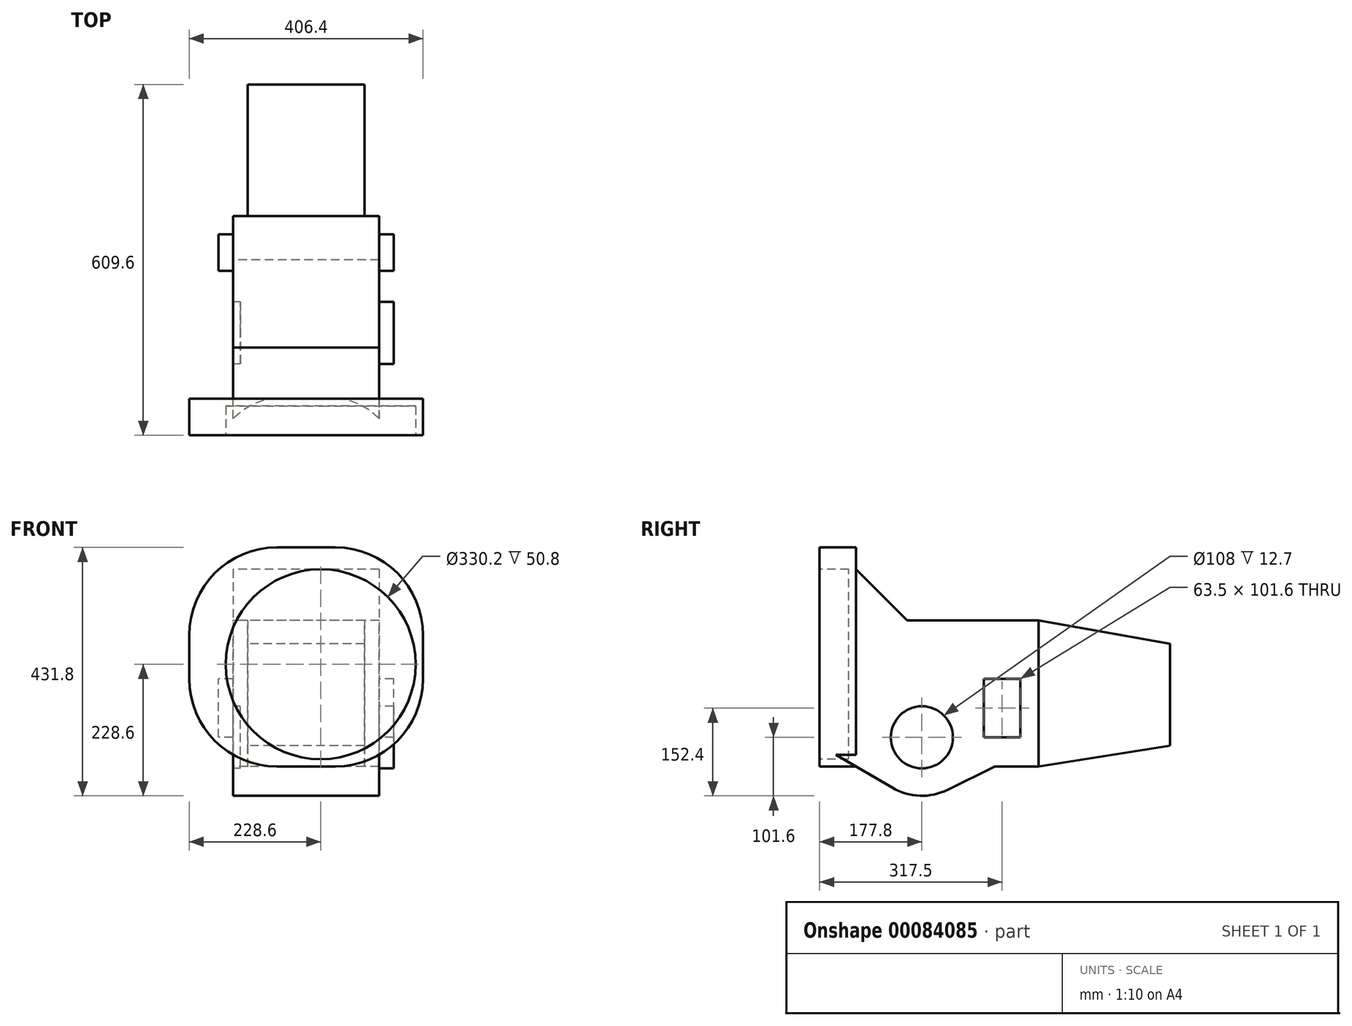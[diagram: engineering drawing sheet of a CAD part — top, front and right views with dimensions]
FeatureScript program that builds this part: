
annotation { "Feature Type Name" : "Feature", "Feature Type Description" : "" }
export const myFeature = defineFeature(function(context is Context, id is Id, definition is map)
    precondition{}
    {
        {
            var Q0;
            Q0=qCreatedBy(makeId("Right.planeOp"),FACE);
            var sketch = newSketch(context, id + "F0", { "sketchPlane" : qUnion([Q0])});
            skCircle(sketch, "E0", {"center": v(0, 0) * mm, "radius": 54 * mm});
            skCircle(sketch, "E1", {"center": v(0, 0) * mm, "radius": 101.6 * mm});
            skLineSegment(sketch, "E2", {"start": v(-177.8, -50.8) * mm, "end": v(-177.8, 330.2) * mm});
            skLineSegment(sketch, "E3", {"start": v(-177.8, -50.8) * mm, "end": v(-114.3, -50.8) * mm});
            skLineSegment(sketch, "E4", {"start": v(-114.3, -50.8) * mm, "end": v(-51.35, -87.67) * mm});
            skLineSegment(sketch, "E5", {"start": v(196.38, -101.6) * mm, "end": v(-238.54, -101.6) * mm, "construction": true});
            skLineSegment(sketch, "E6", {"start": v(-177.8, 330.2) * mm, "end": v(-114.3, 330.2) * mm});
            skLineSegment(sketch, "E7", {"start": v(-114.3, 330.2) * mm, "end": v(-114.3, 292.1) * mm});
            skLineSegment(sketch, "E8", {"start": v(-114.3, 292.1) * mm, "end": v(-25.4, 203.2) * mm});
            skLineSegment(sketch, "E9", {"start": v(-25.4, 203.2) * mm, "end": v(203.2, 203.2) * mm});
            skLineSegment(sketch, "E10", {"start": v(44.8, -91.19) * mm, "end": v(127, -50.8) * mm});
            skLineSegment(sketch, "E11", {"start": v(127, -50.8) * mm, "end": v(203.2, -50.8) * mm});
            skLineSegment(sketch, "E12", {"start": v(203.2, -50.8) * mm, "end": v(203.2, 203.2) * mm});
            skLineSegment(sketch, "E13", {"start": v(203.2, 203.2) * mm, "end": v(431.8, 162.61) * mm});
            skLineSegment(sketch, "E14", {"start": v(431.8, 162.61) * mm, "end": v(431.8, -14.38) * mm});
            skLineSegment(sketch, "E15", {"start": v(431.8, -14.38) * mm, "end": v(203.2, -50.8) * mm});
            skLineSegment(sketch, "E16", {"start": v(-114.3, 292.1) * mm, "end": v(-114.3, -50.8) * mm});
            skLineSegment(sketch, "E17.rect.bottom", {"start": v(171.45, 0) * mm, "end": v(107.95, 0) * mm});
            skLineSegment(sketch, "E17.rect.top", {"start": v(171.45, 101.6) * mm, "end": v(107.95, 101.6) * mm});
            skLineSegment(sketch, "E17.rect.left", {"start": v(171.45, 0) * mm, "end": v(171.45, 101.6) * mm});
            skLineSegment(sketch, "E17.rect.right", {"start": v(107.95, 0) * mm, "end": v(107.95, 101.6) * mm});
            skPoint(sketch, "E17.rect.middle", {"position": v(139.7, 50.8) * mm});
            skSolve(sketch);
        }
        {
            var Q0;
            Q0=makeQuery(id+"F0.imprint","IMPRINT",FACE,{"disambiguationData":[TD([[makeQuery(id+"F0.imprint","IMPRINT",EDGE,{"derivedFrom":sQuery(id+"F0.wireOp",EDGE,"E2")}),-1.0]])]});
            extrude(context, id + "F1", {"entities" : qUnion([Q0]), "depth" : 203.2 * mm, "hasSecondDirection" : true, "secondDirectionOppositeDirection" : true, "secondDirectionDepth" : 203.2 * mm});
        }
        {
            var Q0;
            {var subQ1=sQuery(id+"F0.wireOp",EDGE,"E4");Q0=makeQuery(id+"F0.imprint","IMPRINT",FACE,{"disambiguationData":[TD([[makeQuery(id+"F0.imprint","IMPRINT",EDGE,{"derivedFrom":subQ1}),1.0]])]});}
            var Q1;
            Q1=makeQuery(id+"F0.imprint","IMPRINT",FACE,{"disambiguationData":[TD([[makeQuery(id+"F0.imprint","IMPRINT",EDGE,{"derivedFrom":sQuery(id+"F0.wireOp",EDGE,"E0")}),-1.0]])]});
            extrude(context, id + "F2", {"entities" : qUnion([Q0, Q1]), "operationType" : NewBodyOperationType.ADD, "depth" : 127 * mm, "hasSecondDirection" : true, "secondDirectionOppositeDirection" : true, "secondDirectionDepth" : 127 * mm});
        }
        {
            var Q0;
            Q0=makeQuery(id+"F0.imprint","IMPRINT",FACE,{"disambiguationData":[TD([[makeQuery(id+"F0.imprint","IMPRINT",EDGE,{"derivedFrom":sQuery(id+"F0.wireOp",EDGE,"E12")}),-1.0]])]});
            extrude(context, id + "F3", {"entities" : qUnion([Q0]), "operationType" : NewBodyOperationType.ADD, "depth" : 101.6 * mm, "hasSecondDirection" : true, "secondDirectionOppositeDirection" : true, "secondDirectionDepth" : 101.6 * mm});
        }
        {
            var Q0;
            Q0=makeQuery(id+"F0.imprint","IMPRINT",FACE,{"disambiguationData":[TD([[makeQuery(id+"F0.imprint","IMPRINT",EDGE,{"derivedFrom":sQuery(id+"F0.wireOp",EDGE,"E0")}),1.0]])]});
            extrude(context, id + "F4", {"entities" : qUnion([Q0]), "operationType" : NewBodyOperationType.ADD, "depth" : 152.4 * mm, "hasSecondDirection" : true, "secondDirectionOppositeDirection" : true, "secondDirectionDepth" : 114.3 * mm});
        }
        {
            var Q0;
            Q0=makeQuery(id+"F1.opExtrude","CAP_EDGE",EDGE,{"disambiguationData":[OSD([sQuery(id+"F0.wireOp",EDGE,"E6")])],"isStart":false});
            var Q1;
            Q1=makeQuery(id+"F1.opExtrude","CAP_EDGE",EDGE,{"disambiguationData":[OSD([sQuery(id+"F0.wireOp",EDGE,"E6")])],"isStart":true});
            var Q2;
            Q2=makeQuery(id+"F1.opExtrude","CAP_EDGE",EDGE,{"disambiguationData":[OSD([sQuery(id+"F0.wireOp",EDGE,"E3")])],"isStart":false});
            var Q3;
            Q3=makeQuery(id+"F1.opExtrude","CAP_EDGE",EDGE,{"disambiguationData":[OSD([sQuery(id+"F0.wireOp",EDGE,"E3")])],"isStart":true});
            fillet(context, id + "F5", {"entities" : qUnion([Q0, Q1, Q2, Q3]), "radius" : 152.4 * mm, "tangentPropagation" : true, "allowEdgeOverflow" : false});
        }
        {
            var Q0;
            Q0=makeQuery(id+"F0.imprint","IMPRINT",FACE,{"disambiguationData":[TD([[makeQuery(id+"F0.imprint","IMPRINT",EDGE,{"derivedFrom":sQuery(id+"F0.wireOp",EDGE,"E17.rect.bottom")}),-1.0]])]});
            extrude(context, id + "F6", {"entities" : qUnion([Q0]), "operationType" : NewBodyOperationType.ADD, "depth" : 152.4 * mm, "hasSecondDirection" : true, "secondDirectionOppositeDirection" : true, "secondDirectionDepth" : 152.4 * mm});
        }
        {
            var Q0;
            Q0=makeQuery(id+"F1.opExtrude","SWEPT_FACE",FACE,{"disambiguationData":[OSD([sQuery(id+"F0.wireOp",EDGE,"E2")])]});
            var sketch = newSketch(context, id + "F7", { "sketchPlane" : qUnion([Q0])});
            skCircle(sketch, "E18", {"center": v(25.4, 127) * mm, "radius": 165.1 * mm});
            skSolve(sketch);
        }
        {
            var Q0;
            Q0=makeQuery(id+"F7.imprint","IMPRINT",FACE,{"disambiguationData":[TD([[makeQuery(id+"F7.imprint","IMPRINT",EDGE,{"derivedFrom":sQuery(id+"F7.wireOp",EDGE,"E18")}),1.0]])]});
            extrude(context, id + "F8", {"entities" : qUnion([Q0]), "operationType" : NewBodyOperationType.REMOVE, "oppositeDirection" : true, "depth" : 50.8 * mm});
        }
    });
